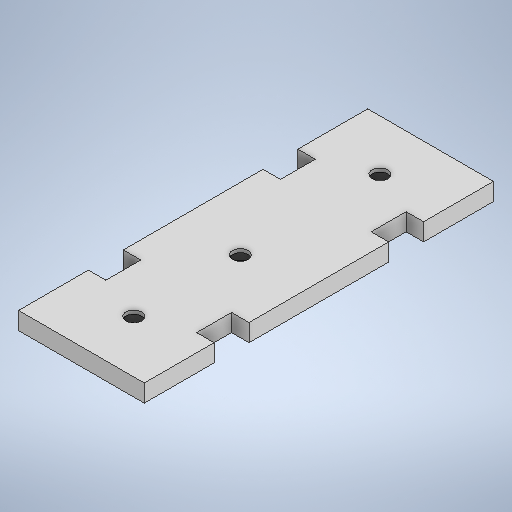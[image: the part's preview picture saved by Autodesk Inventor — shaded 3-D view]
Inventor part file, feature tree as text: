
AUTODESK INVENTOR PART (.ipt)
format: ipt  version: 2025.2 (Build 292293000, 293)  size: 267,776 bytes
history: native  units: mm
features: extrude x2, sketch x2
ambient origin geometry x8: Origin, YZ Plane, XZ Plane, XY Plane, X Axis, Y Axis, Z Axis, Center Point
bodies: Solid1 (feature_tree)
feature tree (4):
  extrude  "Extrusion1"  Depth=100.0mm
  extrude  "Extrusion2"  Depth=20.0mm
  sketch  "Sketch2"  dims[d0=36.0mm d1=100.0mm]
  sketch  "Sketch3"  dims[d2=20.0mm d3=20.0mm d4=10.0mm d5=5.0mm d6=10.0mm d7=5.0mm d8=5.0mm d9=15.0mm d11=30.5mm d12=10.1mm d13=40.0mm d14=10.1mm d15=5.0mm d16=0.0mm d18=4.5mm d19=4.5mm d20=4.5mm d21=1.0mm d22=0.0mm]
